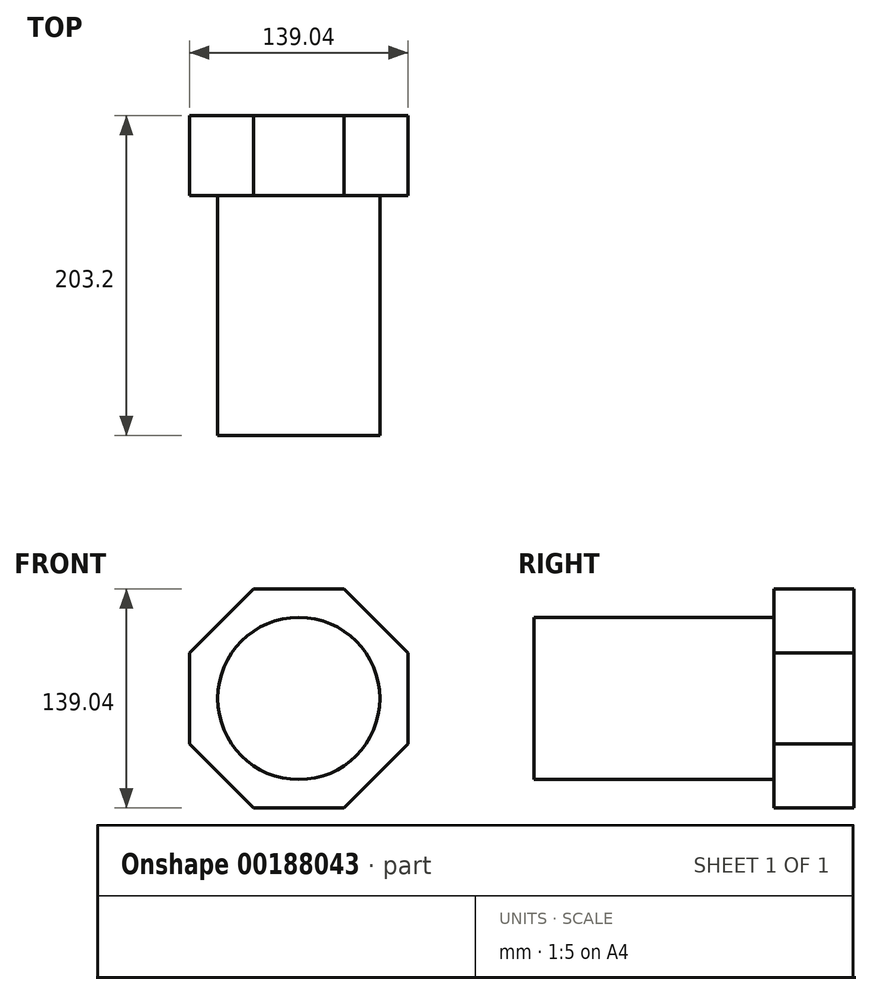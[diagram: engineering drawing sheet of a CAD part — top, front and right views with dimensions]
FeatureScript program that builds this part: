
annotation { "Feature Type Name" : "Feature", "Feature Type Description" : "" }
export const myFeature = defineFeature(function(context is Context, id is Id, definition is map)
    precondition{}
    {
        {
            var Q0;
            Q0=qCreatedBy(makeId("Front.planeOp"),FACE);
            var sketch = newSketch(context, id + "F0", { "sketchPlane" : qUnion([Q0])});
            skCircle(sketch, "E0.cCircle", {"center": v(0, 0) * mm, "radius": 69.52 * mm, "construction": true});
            skLineSegment(sketch, "E0.0", {"start": v(28.8, -69.52) * mm, "end": v(-28.8, -69.52) * mm});
            skLineSegment(sketch, "E0.1", {"start": v(-28.8, -69.52) * mm, "end": v(-69.52, -28.8) * mm});
            skLineSegment(sketch, "E0.2", {"start": v(-69.52, -28.8) * mm, "end": v(-69.52, 28.8) * mm});
            skLineSegment(sketch, "E0.3", {"start": v(-69.52, 28.8) * mm, "end": v(-28.8, 69.52) * mm});
            skLineSegment(sketch, "E0.4", {"start": v(-28.8, 69.52) * mm, "end": v(28.8, 69.52) * mm});
            skLineSegment(sketch, "E0.5", {"start": v(28.8, 69.52) * mm, "end": v(69.52, 28.8) * mm});
            skLineSegment(sketch, "E0.6", {"start": v(69.52, 28.8) * mm, "end": v(69.52, -28.8) * mm});
            skLineSegment(sketch, "E0.7", {"start": v(69.52, -28.8) * mm, "end": v(28.8, -69.52) * mm});
            skPoint(sketch, "E0.0.midPoint", {"position": v(0, -69.52) * mm});
            skLineSegment(sketch, "E1.0", {"start": v(69.52, -69.52) * mm, "end": v(-69.52, -69.52) * mm});
            skLineSegment(sketch, "E1.1", {"start": v(-69.52, -69.52) * mm, "end": v(-69.52, 69.52) * mm});
            skLineSegment(sketch, "E1.2", {"start": v(-69.52, 69.52) * mm, "end": v(69.52, 69.52) * mm});
            skLineSegment(sketch, "E1.3", {"start": v(69.52, 69.52) * mm, "end": v(69.52, -69.52) * mm});
            skSolve(sketch);
        }
        {
            var Q0;
            {var subQ4=sQuery(id+"F0.wireOp",EDGE,"E0.1");Q0=makeQuery(id+"F0.imprint","IMPRINT",FACE,{"disambiguationData":[TD([[makeQuery(id+"F0.imprint","IMPRINT",EDGE,{"derivedFrom":subQ4}),-1.0]])]});}
            extrude(context, id + "F1", {"entities" : qUnion([Q0]), "depth" : 25.4 * mm});
        }
        {
            var Q0;
            Q0=qCreatedBy(makeId("Front.planeOp"),FACE);
            var sketch = newSketch(context, id + "F2", { "sketchPlane" : qUnion([Q0])});
            skCircle(sketch, "E2", {"center": v(0, 0) * mm, "radius": 51.5 * mm});
            skSolve(sketch);
        }
        {
            var Q0;
            Q0 = qSketchRegion(id + "F2", true);
            extrude(context, id + "F3", {"entities" : qUnion([Q0]), "operationType" : NewBodyOperationType.ADD, "depth" : 203.2 * mm});
        }
        {
            var Q0;
            Q0=makeQuery(id+"F1.opExtrude","CAP_FACE",FACE,{"disambiguationData":[OSD([sQuery(id+"F0.wireOp",EDGE,"E0.1"),sQuery(id+"F0.wireOp",EDGE,"E0.3"),sQuery(id+"F0.wireOp",EDGE,"E0.5"),sQuery(id+"F0.wireOp",EDGE,"E0.7"),sQuery(id+"F0.wireOp",EDGE,"E1.0"),sQuery(id+"F0.wireOp",EDGE,"E1.1"),sQuery(id+"F0.wireOp",EDGE,"E1.2"),sQuery(id+"F0.wireOp",EDGE,"E1.3")])],"isStart":false});
            var sketch = newSketch(context, id + "F4", { "sketchPlane" : qUnion([Q0])});
            skCircle(sketch, "E3.cCircle", {"center": v(0, 0) * mm, "radius": 69.52 * mm, "construction": true});
            skLineSegment(sketch, "E3.0", {"start": v(28.8, -69.52) * mm, "end": v(-28.8, -69.52) * mm});
            skLineSegment(sketch, "E3.1", {"start": v(-28.8, -69.52) * mm, "end": v(-69.52, -28.8) * mm});
            skLineSegment(sketch, "E3.2", {"start": v(-69.52, -28.8) * mm, "end": v(-69.52, 28.8) * mm});
            skLineSegment(sketch, "E3.3", {"start": v(-69.52, 28.8) * mm, "end": v(-28.8, 69.52) * mm});
            skLineSegment(sketch, "E3.4", {"start": v(-28.8, 69.52) * mm, "end": v(28.8, 69.52) * mm});
            skLineSegment(sketch, "E3.5", {"start": v(28.8, 69.52) * mm, "end": v(69.52, 28.8) * mm});
            skLineSegment(sketch, "E3.6", {"start": v(69.52, 28.8) * mm, "end": v(69.52, -28.8) * mm});
            skLineSegment(sketch, "E3.7", {"start": v(69.52, -28.8) * mm, "end": v(28.8, -69.52) * mm});
            skPoint(sketch, "E3.0.midPoint", {"position": v(0, -69.52) * mm});
            skSolve(sketch);
        }
        {
            var Q0;
            Q0 = qSketchRegion(id + "F4", true);
            extrude(context, id + "F5", {"entities" : qUnion([Q0]), "operationType" : NewBodyOperationType.ADD, "depth" : 25.4 * mm});
        }
    });
